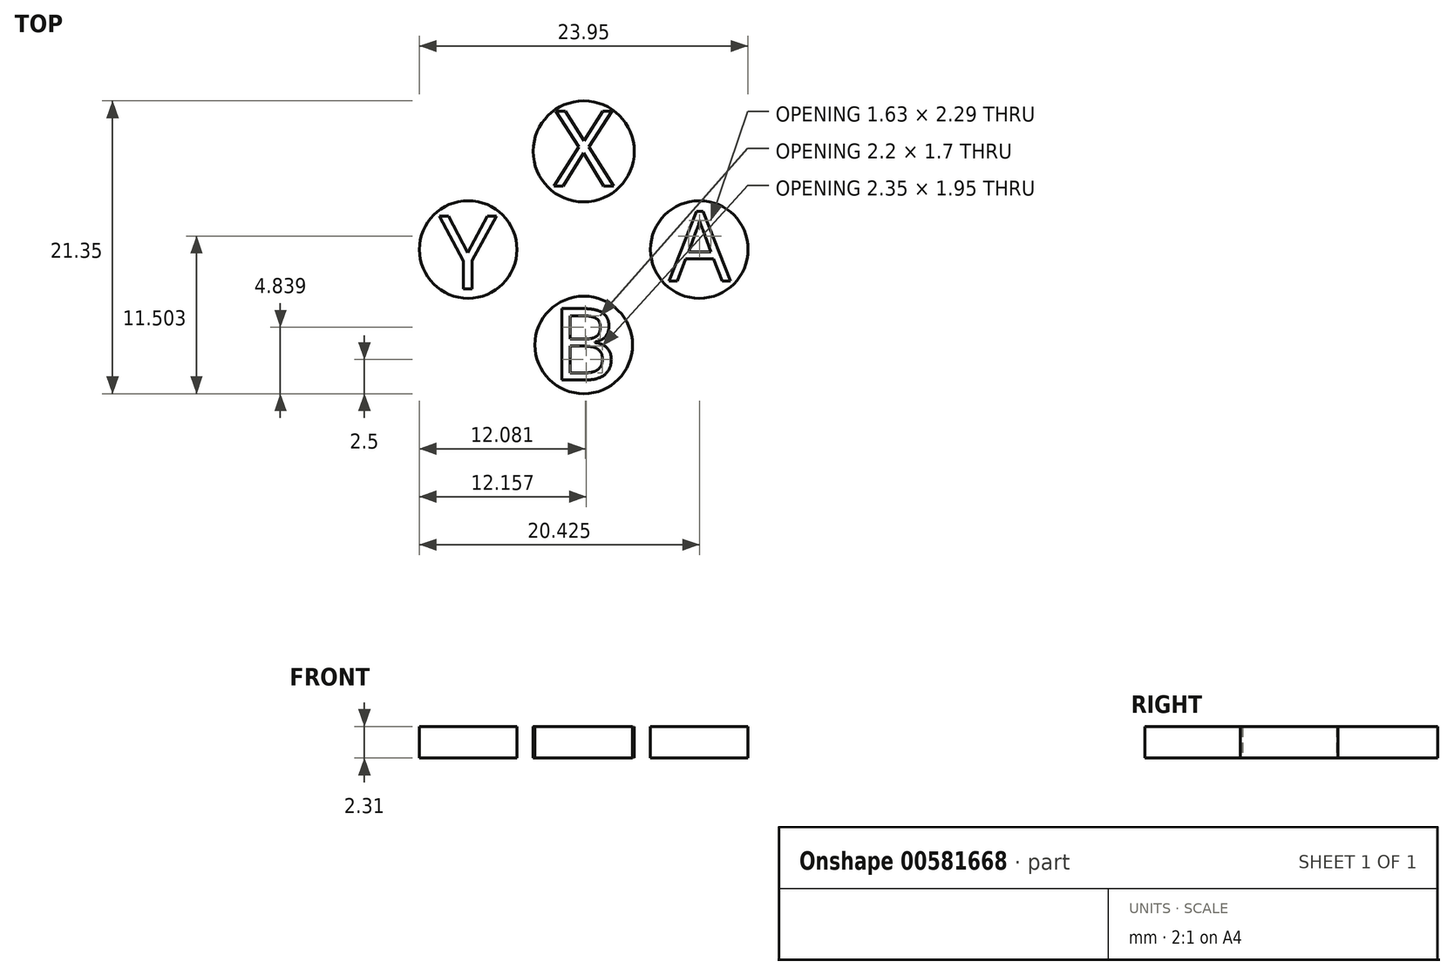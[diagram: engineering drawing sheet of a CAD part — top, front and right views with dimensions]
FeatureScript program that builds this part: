
annotation { "Feature Type Name" : "Feature", "Feature Type Description" : "" }
export const myFeature = defineFeature(function(context is Context, id is Id, definition is map)
    precondition{}
    {
        {
            var Q0;
            Q0=qCreatedBy(makeId("Top.planeOp"),FACE);
            var sketch = newSketch(context, id + "F0", { "sketchPlane" : qUnion([Q0])});
            skCircle(sketch, "E0", {"center": v(-28.45, -20.2) * mm, "radius": 3.68 * mm});
            skCircle(sketch, "E1", {"center": v(-28.45, -34.3) * mm, "radius": 3.56 * mm});
            skCircle(sketch, "E2", {"center": v(-36.87, -27.34) * mm, "radius": 3.56 * mm});
            skCircle(sketch, "E3", {"center": v(-20.03, -27.34) * mm, "radius": 3.56 * mm});
            skSolve(sketch);
        }
        {
            var Q0;
            Q0 = qSketchRegion(id + "F0", true);
            extrude(context, id + "F1", {"entities" : qUnion([Q0]), "depth" : 2.3 * mm, "offsetDistance" : 25.4 * mm});
        }
        {
            var Q0;
            Q0=makeQuery(id+"F1.opExtrude","CAP_FACE",FACE,{"disambiguationData":[OSD([sQuery(id+"F0.wireOp",EDGE,"E0")])],"isStart":false});
            var sketch = newSketch(context, id + "F2", { "sketchPlane" : qUnion([Q0])});
            skText(sketch, "E4", { "text": "X", "fontName": "OpenSans-Regular.ttf"});
            const initialGuessF2  = {"E4": [-0.03064, -0.02272, 1, 0, 0.0055]};
            skSetInitialGuess(sketch, initialGuessF2);
            skSolve(sketch);
        }
        {
            var Q0;
            Q0 = qSketchRegion(id + "F2", true);
            extrude(context, id + "F3", {"entities" : qUnion([Q0]), "depth" : 0.03 * mm, "offsetDistance" : 25.4 * mm});
        }
        {
            var Q0;
            Q0=makeQuery(id+"F1.opExtrude","CAP_FACE",FACE,{"disambiguationData":[OSD([sQuery(id+"F0.wireOp",EDGE,"E3")])],"isStart":false});
            var sketch = newSketch(context, id + "F4", { "sketchPlane" : qUnion([Q0])});
            skText(sketch, "E5", { "text": "A", "fontName": "OpenSans-Regular.ttf"});
            const initialGuessF4  = {"E5": [-0.02223, -0.02963, 1, 0, 0.00508]};
            skSetInitialGuess(sketch, initialGuessF4);
            skSolve(sketch);
        }
        {
            var Q0;
            Q0 = qSketchRegion(id + "F4", true);
            extrude(context, id + "F5", {"entities" : qUnion([Q0]), "depth" : 0.03 * mm, "offsetDistance" : 25.4 * mm});
        }
        {
            var Q0;
            Q0=makeQuery(id+"F1.opExtrude","CAP_FACE",FACE,{"disambiguationData":[OSD([sQuery(id+"F0.wireOp",EDGE,"E2")])],"isStart":false});
            var sketch = newSketch(context, id + "F6", { "sketchPlane" : qUnion([Q0])});
            skText(sketch, "E6", { "text": "Y", "fontName": "OpenSans-Regular.ttf"});
            const initialGuessF6  = {"E6": [-0.03897, -0.03022, 1, 0, 0.00535]};
            skSetInitialGuess(sketch, initialGuessF6);
            skSolve(sketch);
        }
        {
            var Q0;
            Q0 = qSketchRegion(id + "F6", true);
            extrude(context, id + "F7", {"entities" : qUnion([Q0]), "depth" : 0.03 * mm, "offsetDistance" : 25.4 * mm});
        }
        {
            var Q0;
            Q0=makeQuery(id+"F1.opExtrude","CAP_FACE",FACE,{"disambiguationData":[OSD([sQuery(id+"F0.wireOp",EDGE,"E1")])],"isStart":false});
            var sketch = newSketch(context, id + "F8", { "sketchPlane" : qUnion([Q0])});
            skText(sketch, "E7", { "text": "B", "fontName": "OpenSans-Regular.ttf"});
            const initialGuessF8  = {"E7": [-0.03076, -0.03685, 1, 0, 0.00525]};
            skSetInitialGuess(sketch, initialGuessF8);
            skSolve(sketch);
        }
        {
            var Q0;
            Q0 = qSketchRegion(id + "F8", true);
            extrude(context, id + "F9", {"entities" : qUnion([Q0]), "depth" : 0.03 * mm, "offsetDistance" : 25.4 * mm});
        }
    });
